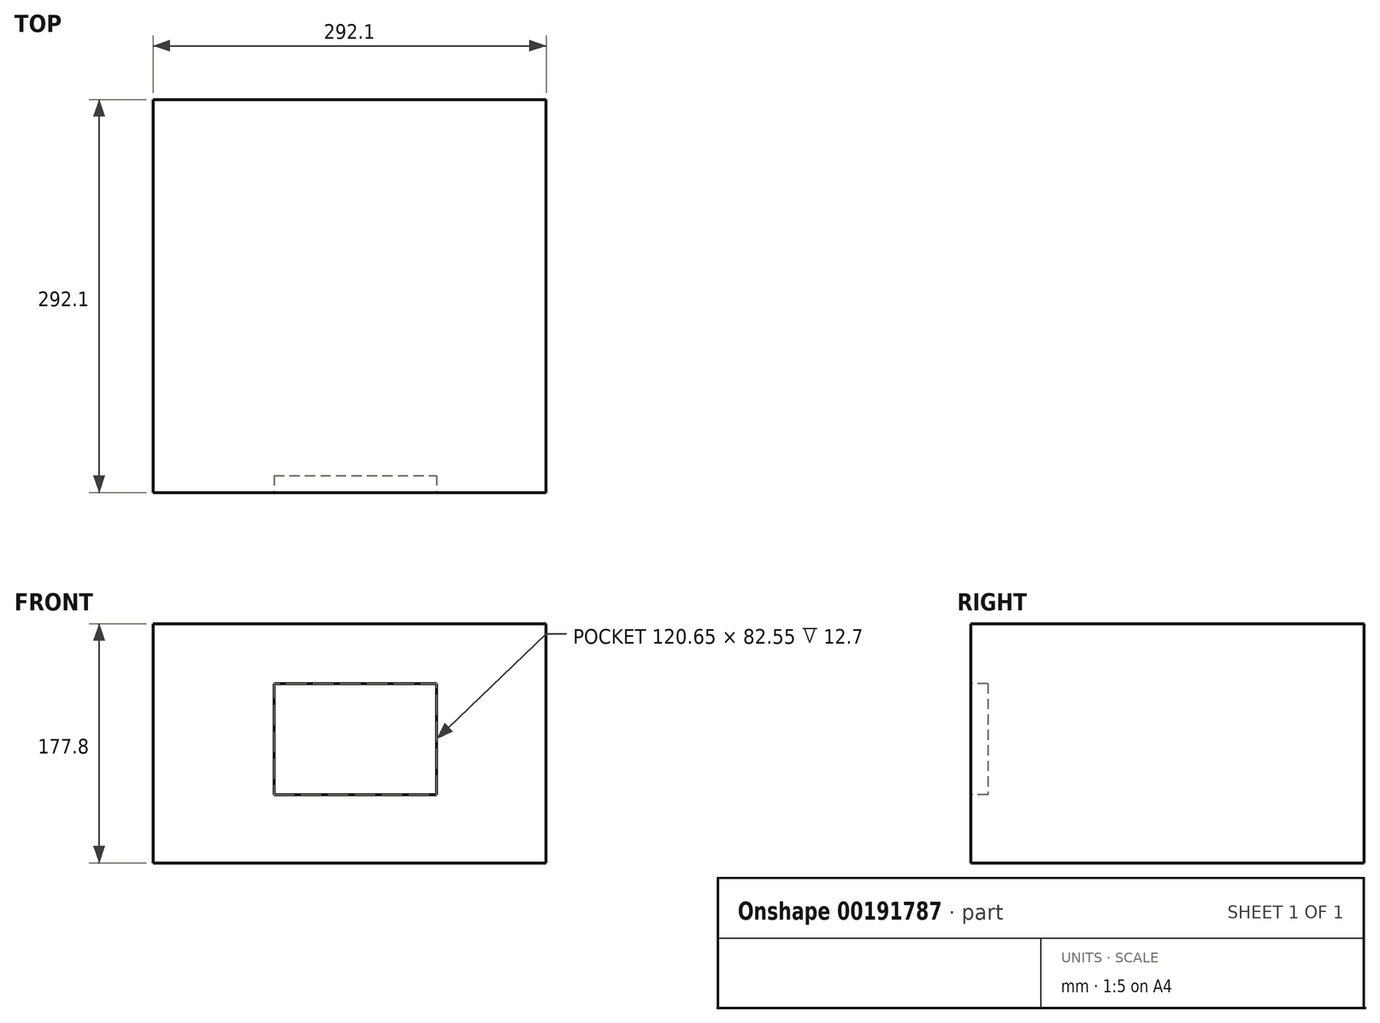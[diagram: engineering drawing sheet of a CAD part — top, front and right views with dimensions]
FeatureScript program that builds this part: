
annotation { "Feature Type Name" : "Feature", "Feature Type Description" : "" }
export const myFeature = defineFeature(function(context is Context, id is Id, definition is map)
    precondition{}
    {
        {
            var Q0;
            Q0=qCreatedBy(makeId("Front.planeOp"),FACE);
            var sketch = newSketch(context, id + "F0", { "sketchPlane" : qUnion([Q0])});
            skLineSegment(sketch, "E0.bottom", {"start": v(-148.5, 76.47) * mm, "end": v(143.6, 76.47) * mm});
            skLineSegment(sketch, "E0.top", {"start": v(-148.5, -101.33) * mm, "end": v(143.6, -101.33) * mm});
            skLineSegment(sketch, "E0.left", {"start": v(-148.5, 76.47) * mm, "end": v(-148.5, -101.33) * mm});
            skLineSegment(sketch, "E0.right", {"start": v(143.6, 76.47) * mm, "end": v(143.6, -101.33) * mm});
            skSolve(sketch);
        }
        {
            var Q0;
            Q0 = qSketchRegion(id + "F0", true);
            extrude(context, id + "F1", {"entities" : qUnion([Q0]), "depth" : 292.1 * mm, "offsetDistance" : 25.4 * mm});
        }
        {
            var Q0;
            Q0=makeQuery(id+"F1.opExtrude","CAP_FACE",FACE,{"disambiguationData":[OSD([sQuery(id+"F0.wireOp",EDGE,"E0.bottom"),sQuery(id+"F0.wireOp",EDGE,"E0.top"),sQuery(id+"F0.wireOp",EDGE,"E0.left"),sQuery(id+"F0.wireOp",EDGE,"E0.right")])],"isStart":false});
            var sketch = newSketch(context, id + "F2", { "sketchPlane" : qUnion([Q0])});
            skLineSegment(sketch, "E1.bottom", {"start": v(-58.53, 32.02) * mm, "end": v(62.12, 32.02) * mm});
            skLineSegment(sketch, "E1.top", {"start": v(-58.53, -50.53) * mm, "end": v(62.12, -50.53) * mm});
            skLineSegment(sketch, "E1.left", {"start": v(-58.53, 32.02) * mm, "end": v(-58.53, -50.53) * mm});
            skLineSegment(sketch, "E1.right", {"start": v(62.12, 32.02) * mm, "end": v(62.12, -50.53) * mm});
            skSolve(sketch);
        }
        {
            var Q0;
            Q0 = qSketchRegion(id + "F2", true);
            extrude(context, id + "F3", {"entities" : qUnion([Q0]), "operationType" : NewBodyOperationType.REMOVE, "oppositeDirection" : true, "depth" : 12.7 * mm, "offsetDistance" : 25.4 * mm});
        }
    });
